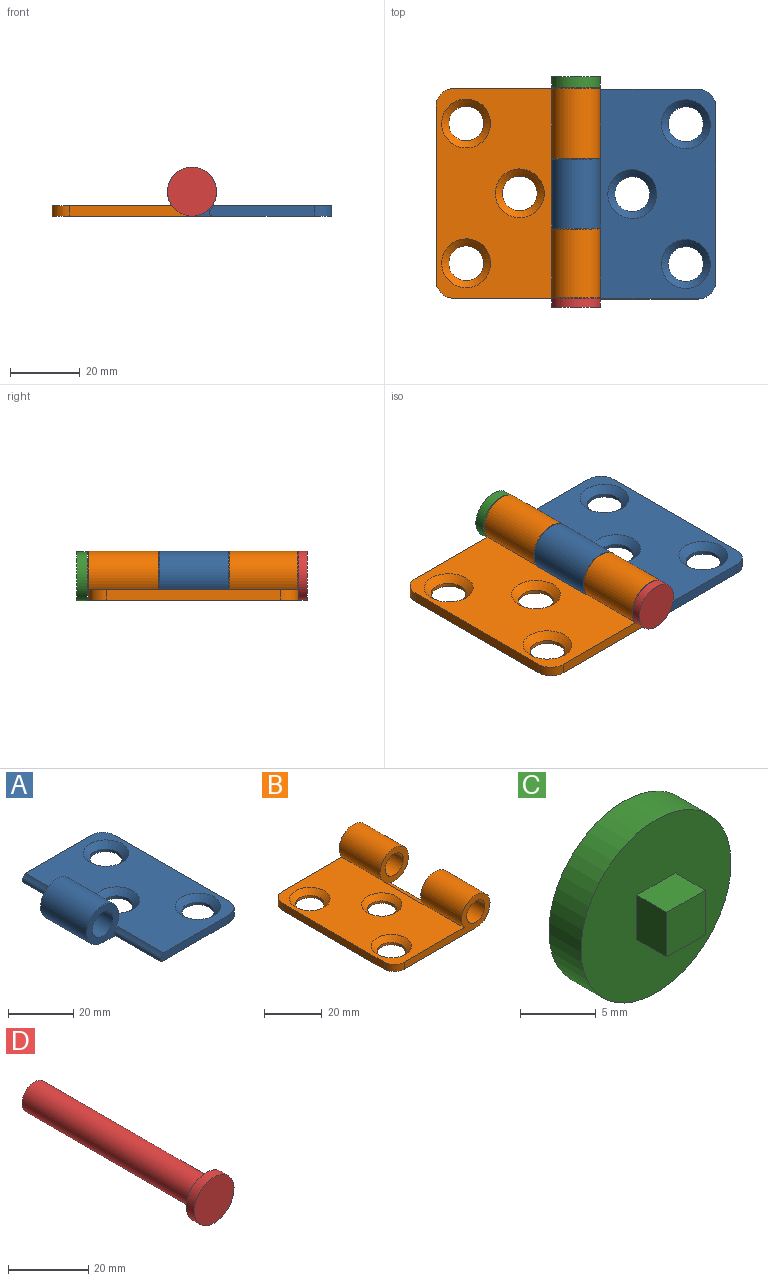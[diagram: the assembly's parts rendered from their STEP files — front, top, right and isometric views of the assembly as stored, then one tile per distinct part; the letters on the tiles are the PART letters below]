
ASSEMBLY  parts=4 mates=3
PART A: 21 faces, bbox 47x60x14 mm
  f0: cylinder r=7mm len=20mm, axis (0,1,0), area 744.9mm2, adj f1,f3,f9,f11
  f1: plane 60x40mm, normal (0,0,-1), area 1917.9mm2, adj f0,f2,f4,f5,f6,f7,f8,f9
  f2: plane 50x3mm, normal (1,0,0), area 150mm2, adj f1,f3,f19,f20
  f3: plane 60x34.26mm, normal (0,0,1), area 1563mm2, adj f0,f2,f4,f5,f9,f10,f11,f12
  f4: plane 30.11x3mm, normal (0,-1,0), area 88.9mm2, adj f1,f3,f10,f14,f20
  f5: plane 30.11x3mm, normal (0,1,0), area 88.9mm2, adj f1,f3,f12,f15,f19
  f6: cylinder r=5mm len=10mm, axis (0,0,1), area 31.4mm2, adj f1,f18
  f7: cylinder r=5mm len=10mm, axis (0,0,1), area 31.4mm2, adj f1,f17
  f8: cylinder r=5mm len=10mm, axis (0,0,1), area 31.4mm2, adj f1,f16
  f9: plane 14x14mm, normal (0,-1,0), area 94.3mm2, adj f0,f1,f3,f10,f13,f14
  f10: cylinder r=7.41mm len=20mm, axis (0,-1,0), area 33.2mm2, adj f3,f4,f9,f14
  f11: plane 14x14mm, normal (0,1,0), area 94.3mm2, adj f0,f1,f3,f12,f13,f15
  f12: cylinder r=7.41mm len=20mm, axis (0,-1,0), area 33.2mm2, adj f3,f5,f11,f15
  f13: cylinder r=4.5mm len=20mm, axis (0,1,0), area 565.5mm2, adj f9,f11
  f14: cylinder r=1mm len=20mm, axis (0,-1,0), area 47.3mm2, adj f1,f4,f9,f10
  f15: cylinder r=1mm len=20mm, axis (0,-1,0), area 47.3mm2, adj f1,f5,f11,f12
  f16: cone r=5mm half-angle=45deg, axis (0,0,1), area 106.6mm2, adj f3,f8
  f17: cone r=5mm half-angle=45deg, axis (0,0,1), area 106.6mm2, adj f3,f7
  f18: cone r=5mm half-angle=45deg, axis (0,0,1), area 106.6mm2, adj f3,f6
  f19: cylinder r=5mm len=5mm, axis (0,0,1), area 23.6mm2, adj f1,f2,f3,f5
  f20: cylinder r=5mm len=5mm, axis (0,0,-1), area 23.6mm2, adj f1,f2,f3,f4
PART B: 20 faces, bbox 47x60x14 mm
  f0: plane 60x40mm, normal (0,0,-1), area 2119mm2, adj f3,f4,f6,f7,f8,f9,f10,f11
  f1: plane 60x34.26mm, normal (0,0,1), area 1577.7mm2, adj f3,f4,f6,f7,f8,f12,f13,f14
  f2: cylinder r=4.5mm len=20mm, axis (0,1,0), area 565.5mm2, adj f8,f13
  f3: cylinder r=7mm len=20mm, axis (0,1,0), area 744.9mm2, adj f0,f1,f8,f13
  f4: plane 50x3mm, normal (-1,0,0), area 150mm2, adj f0,f1,f18,f19
  f5: cylinder r=4.5mm len=20mm, axis (0,1,0), area 565.5mm2, adj f7,f14
  f6: cylinder r=7mm len=20mm, axis (0,1,0), area 744.9mm2, adj f0,f1,f7,f14
  f7: plane 42x14mm, normal (0,-1,0), area 183.2mm2, adj f0,f1,f5,f6,f19
  f8: plane 42x14mm, normal (0,1,0), area 183.2mm2, adj f0,f1,f2,f3,f18
  f9: cylinder r=5mm len=10mm, axis (0,0,1), area 31.4mm2, adj f0,f15
  f10: cylinder r=5mm len=10mm, axis (0,0,1), area 31.4mm2, adj f0,f17
  f11: cylinder r=5mm len=10mm, axis (0,0,1), area 31.4mm2, adj f0,f16
  f12: cylinder r=7.21mm len=20mm, axis (0,-1,0), area 106.8mm2, adj f0,f1,f13,f14
  f13: plane 14x14mm, normal (0,-1,0), area 91.5mm2, adj f0,f1,f2,f3,f12
  f14: plane 14x14mm, normal (0,1,0), area 91.5mm2, adj f0,f1,f5,f6,f12
  f15: cone r=7mm half-angle=45deg, axis (0,0,1), area 106.6mm2, adj f1,f9
  f16: cone r=7mm half-angle=45deg, axis (0,0,1), area 106.6mm2, adj f1,f11
  f17: cone r=7mm half-angle=45deg, axis (0,0,1), area 106.6mm2, adj f1,f10
  f18: cylinder r=5mm len=5mm, axis (0,0,1), area 23.6mm2, adj f0,f1,f4,f8
  f19: cylinder r=5mm len=5mm, axis (0,0,-1), area 23.6mm2, adj f0,f1,f4,f7
PART C: 8 faces, bbox 14x5.8x14 mm
  f0: plane 3.6x2.8mm, normal (0,0,-1), area 10.1mm2, adj f1,f3,f4,f5
  f1: plane 3.6x2.8mm, normal (-1,0,0), area 10.1mm2, adj f0,f2,f4,f5
  f2: plane 3.6x2.8mm, normal (0,0,1), area 10.1mm2, adj f1,f3,f4,f5
  f3: plane 3.6x2.8mm, normal (1,0,0), area 10.1mm2, adj f0,f2,f4,f5
  f4: plane 3.6x3.6mm, normal (0,-1,0), area 13mm2, adj f0,f1,f2,f3
  f5: plane 14x14mm, normal (0,-1,0), area 141mm2, adj f0,f1,f2,f3,f6
  f6: cylinder r=7mm len=14mm, axis (0,-1,0), area 131.9mm2, adj f5,f7
  f7: plane 14x14mm, normal (0,1,0), area 153.9mm2, adj f6
PART D: 10 faces, bbox 14x63.2x14 mm
  f0: plane 8.8x8.8mm, normal (0,1,0), area 44.8mm2, adj f1,f5,f6,f7,f8
  f1: cylinder r=4.4mm len=60.4mm, axis (0,-1,0), area 1669.8mm2, adj f0,f4
  f2: cylinder r=7mm len=14mm, axis (0,1,0), area 123.2mm2, adj f3,f4
  f3: plane 14x14mm, normal (0,-1,0), area 153.9mm2, adj f2
  f4: plane 14x14mm, normal (0,1,0), area 93.1mm2, adj f1,f2
  f5: plane 4x3mm, normal (0,0,1), area 12mm2, adj f0,f6,f8,f9
  f6: plane 4x3mm, normal (1,0,0), area 12mm2, adj f0,f5,f7,f9
  f7: plane 4x3mm, normal (0,0,-1), area 12mm2, adj f0,f6,f8,f9
  f8: plane 4x3mm, normal (-1,0,0), area 12mm2, adj f0,f5,f7,f9
  f9: plane 4x4mm, normal (0,1,0), area 16mm2, adj f5,f6,f7,f8
PLACE A t=(0.39,16.6,18.81)mm
PLACE B t=(0.39,16.8,18.81)mm
PLACE C t=(0.39,17,18.61)mm
PLACE D t=(0.39,17.2,18.81)mm
MATE revolute D.f2 <-> B.f2  axis (0,1,0) through (0.39,-43,25.81)mm
MATE revolute B.f2 <-> A.f13  axis (0,-1,0) through (0.39,-3.2,25.81)mm
MATE fastened D.f2 <-> C.f4  axis (0,1,0) through (0.39,14.4,25.81)mm
